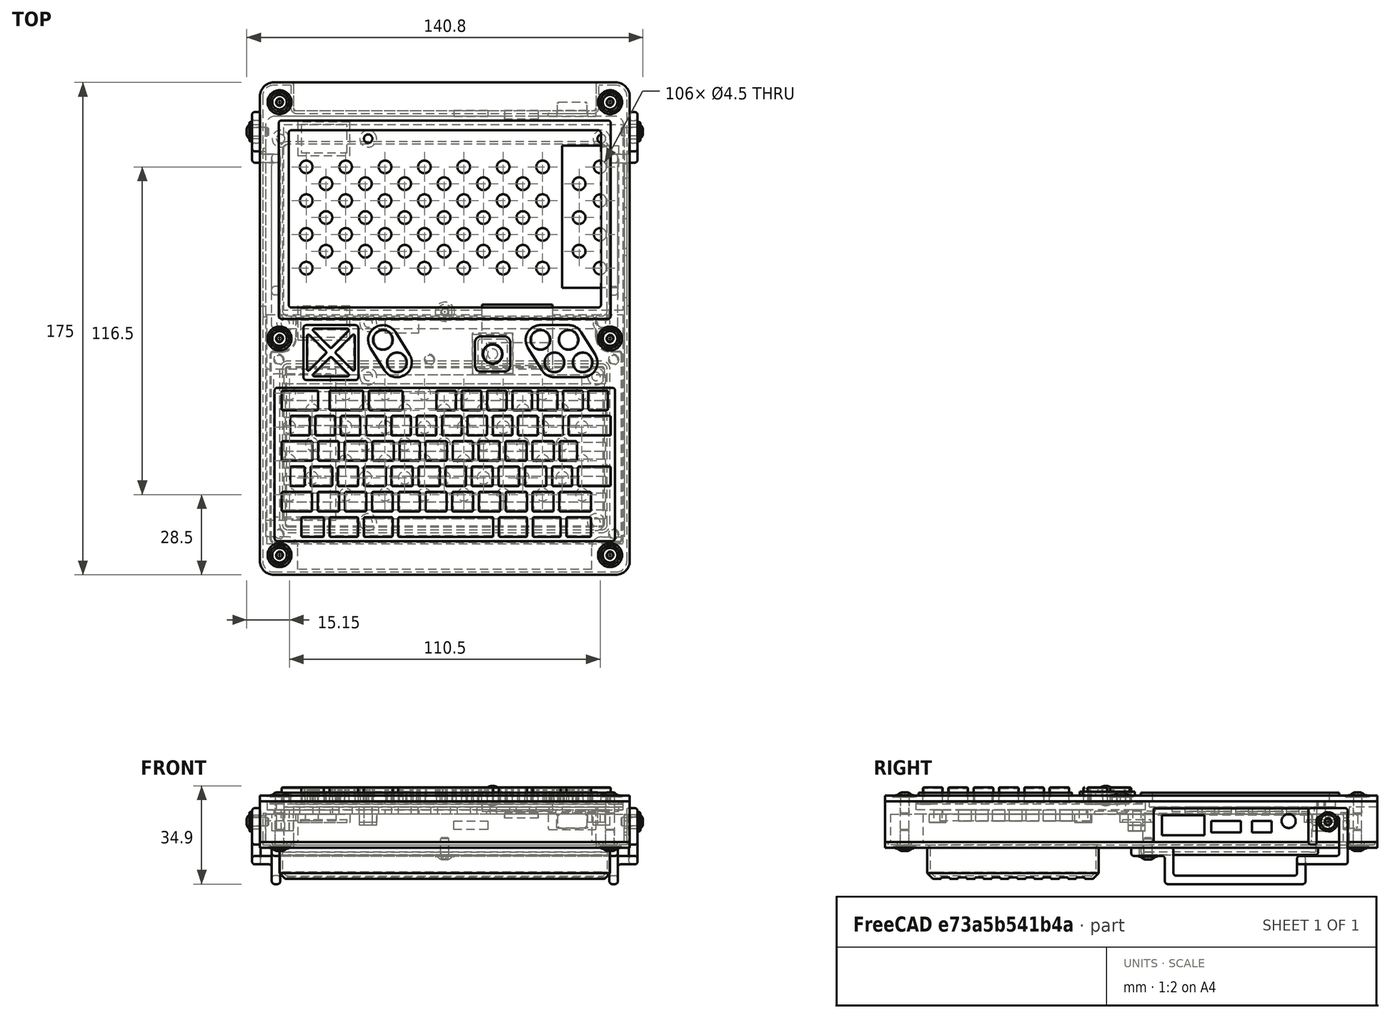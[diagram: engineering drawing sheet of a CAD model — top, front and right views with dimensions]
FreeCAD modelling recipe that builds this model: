
FCSTD DOCUMENT  (FreeCAD 0.20R29603 (Git))
Label: assembly
License: All rights reserved
LicenseURL: http://en.wikipedia.org/wiki/All_rights_reserved
objects: Part::FeaturePython×13, Part::Feature×8, Image::ImagePlane×1, App::Part×1
note: 21 computed .brp shape members not serialized (recipe doc carries the construction recipe); baked Part::Feature solids carry a one-line shape summary decoded from their .brp

FEATURE [Part::Feature] Pocket002001002001001  label="enclosure_top"
  Placement = pos=(0,0,-10) rot=(0,0,1;0rad)
  shape: bbox 131.5 x 175 x 3.5 mm, 630 faces (baked)
FEATURE [Part::Feature] Pocket002001002001002  label="enclosure_bottom"
  Placement = pos=(0,0,2) rot=(0,0,1;0rad)
  shape: bbox 131.5 x 175 x 13 mm, 176 faces (baked)
FEATURE [Part::Feature] Thickness001001  label="keypad"
  Placement = pos=(0.5,-36,8.5) rot=(0,0,1;0rad)
  shape: bbox 125 x 80 x 6.002 mm, 2875 faces (baked)
FEATURE [Part::Feature] Fusion001001  label="trackball"
  Placement = pos=(17,-9,13.5) rot=(0,0,1;0rad)
  shape: bbox 10.66 x 10.66 x 7 mm, 20 faces (baked)
FEATURE [Part::Feature] Pocket002001001  label="enclosure_body"
  shape: bbox 137.5 x 175 x 14.5 mm, 265 faces (baked)
FEATURE [Part::Feature] Fillet001001001  label="button"
  Placement = pos=(45.3,75.5,7.5) rot=(1,0,0;4.71239rad)
  shape: bbox 17 x 5 x 6 mm, 27 faces (baked)
FEATURE [Image::ImagePlane] ImagePlane  label="screen"
  Placement = pos=(3.5,39,14.4) rot=(0,0,1;0rad)
  XSize = 120.132
  YSize = 65.3426
FEATURE [Part::FeaturePython] Screw  label="M3x6-Screw"  # Fasteners workbench fastener (typed FeaturePython)
  Placement = pos=(-58.75,80.5,16) rot=(0,0,1;0rad)
  baseObject = -> Pocket002001002001001 [Edge581]
  diameter = 1
  invert = true
  leftHanded = false
  length = 0
  lengthCustom = 6
  matchOuter = false
  offset = 0
  thread = false
  type = 52
FEATURE [Part::FeaturePython] Screw001  label="M3x6-Screw009"  # Fasteners workbench fastener (typed FeaturePython)
  Placement = pos=(58.75,80.5,16) rot=(0,0,1;0rad)
  baseObject = -> Pocket002001002001001 [Edge583]
  diameter = 1
  invert = true
  leftHanded = false
  length = 0
  lengthCustom = 6
  matchOuter = false
  offset = 0
  thread = false
  type = 52
FEATURE [Part::FeaturePython] Screw002  label="M3x6-Screw008"  # Fasteners workbench fastener (typed FeaturePython)
  Placement = pos=(58.75,-3.5,16) rot=(0,0,1;0rad)
  baseObject = -> Pocket002001002001001 [Edge1287]
  diameter = 1
  invert = false
  leftHanded = false
  length = 0
  lengthCustom = 6
  matchOuter = false
  offset = 0
  thread = false
  type = 52
FEATURE [Part::FeaturePython] Screw003  label="M3x6-Screw007"  # Fasteners workbench fastener (typed FeaturePython)
  Placement = pos=(-58.75,-3.5,16) rot=(0,0,1;0rad)
  baseObject = -> Pocket002001002001001 [Edge601]
  diameter = 1
  invert = false
  leftHanded = false
  length = 0
  lengthCustom = 6
  matchOuter = false
  offset = 0
  thread = false
  type = 52
FEATURE [Part::FeaturePython] Screw004  label="M3x6-Screw004"  # Fasteners workbench fastener (typed FeaturePython)
  Placement = pos=(-58.75,-80.5,16) rot=(0,0,1;0rad)
  baseObject = -> Pocket002001002001001 [Edge927]
  diameter = 1
  invert = true
  leftHanded = false
  length = 0
  lengthCustom = 6
  matchOuter = false
  offset = 0
  thread = false
  type = 52
FEATURE [Part::FeaturePython] Screw005  label="M3x6-Screw005"  # Fasteners workbench fastener (typed FeaturePython)
  Placement = pos=(58.75,-80.5,16) rot=(0,0,1;0rad)
  baseObject = -> Pocket002001002001001 [Edge1691]
  diameter = 1
  invert = true
  leftHanded = false
  length = 0
  lengthCustom = 6
  matchOuter = false
  offset = 0
  thread = false
  type = 52
FEATURE [Part::FeaturePython] Screw006  label="M3x6-Screw010"  # Fasteners workbench fastener (typed FeaturePython)
  Placement = pos=(58.75,80.5,-1.5) rot=(-1,0,0;3.14159rad)
  baseObject = -> Pocket002001002001002 [Edge275]
  diameter = 1
  invert = true
  leftHanded = false
  length = 0
  lengthCustom = 6
  matchOuter = false
  offset = 0
  thread = false
  type = 52
FEATURE [Part::FeaturePython] Screw007  label="M3x6-Screw011"  # Fasteners workbench fastener (typed FeaturePython)
  Placement = pos=(-58.75,80.5,-1.5) rot=(-1,0,0;3.14159rad)
  baseObject = -> Pocket002001002001002 [Edge241]
  diameter = 1
  invert = true
  leftHanded = false
  length = 0
  lengthCustom = 6
  matchOuter = false
  offset = 0
  thread = false
  type = 52
FEATURE [Part::FeaturePython] Screw008  label="M3x6-Screw012"  # Fasteners workbench fastener (typed FeaturePython)
  Placement = pos=(58.75,-80.5,-1.5) rot=(-1,0,0;3.14159rad)
  baseObject = -> Pocket002001002001002 [Edge279]
  diameter = 1
  invert = true
  leftHanded = false
  length = 0
  lengthCustom = 6
  matchOuter = false
  offset = 0
  thread = false
  type = 52
FEATURE [Part::FeaturePython] Screw009  label="M3x6-Screw013"  # Fasteners workbench fastener (typed FeaturePython)
  Placement = pos=(-58.75,-80.5,-1.5) rot=(-1,0,0;3.14159rad)
  baseObject = -> Pocket002001002001002 [Edge277]
  diameter = 1
  invert = true
  leftHanded = false
  length = 0
  lengthCustom = 6
  matchOuter = false
  offset = 0
  thread = false
  type = 52
FEATURE [Part::Feature] Fillet001001  label="kickstand"
  Placement = pos=(0,-8e-16,-3.4) rot=(1,0,0;4.71239rad)
  shape: bbox 137 x 77 x 27 mm, 242 faces (baked)
FEATURE [Part::FeaturePython] Screw010  label="M3x6-Screw014"  # Fasteners workbench fastener (typed FeaturePython)
  Placement = pos=(68.75,70,7.25) rot=(0,1,0;1.5708rad)
  baseObject = -> Pocket002001001 [Edge366]
  diameter = 1
  invert = true
  leftHanded = false
  length = 0
  lengthCustom = 6
  matchOuter = false
  offset = 0
  thread = false
  type = 52
FEATURE [Part::FeaturePython] Screw011  label="M3x6-Screw015"  # Fasteners workbench fastener (typed FeaturePython)
  Placement = pos=(0,6,-4.5) rot=(-1,0,0;3.14159rad)
  baseObject = -> Pocket002001002001002 [Edge39]
  diameter = 1
  invert = false
  leftHanded = false
  length = 0
  lengthCustom = 6
  matchOuter = false
  offset = 0
  thread = false
  type = 52
FEATURE [Part::FeaturePython] Screw012  label="M3x6-Screw016"  # Fasteners workbench fastener (typed FeaturePython)
  Placement = pos=(-68.75,70,7.25) rot=(0,-1,0;1.5708rad)
  baseObject = -> Pocket002001001 [Edge324]
  diameter = 1
  invert = false
  leftHanded = false
  length = 0
  lengthCustom = 6
  matchOuter = false
  offset = 0
  thread = false
  type = 52
FEATURE [App::Part] Part  label="fasteners"
  Group = -> [Screw,Screw001,Screw002,Screw003,Screw004,Screw005,Screw006,Screw007,Screw008,Screw009,Screw010,Screw011,Screw012]
  Origin = -> Origin
FEATURE [Part::Feature] Fillet001  label="expansion_plate"
  Placement = pos=(-64.6,34.2,5.1) rot=(-0.57735,-0.57735,-0.57735;4.18879rad)
  shape: bbox 1 x 60 x 10.5 mm, 10 faces (baked)
